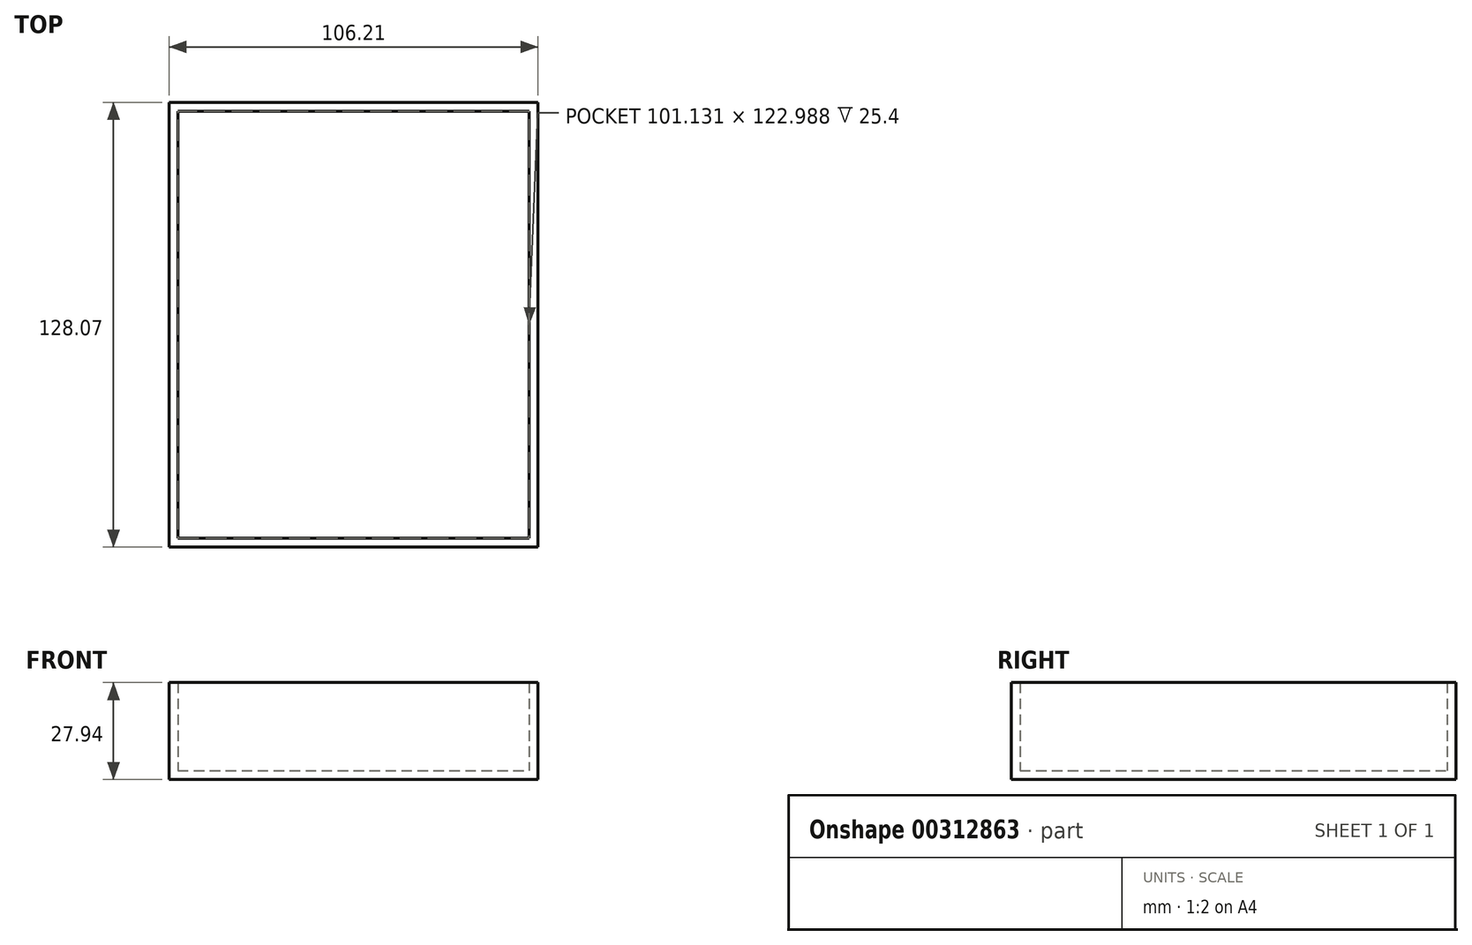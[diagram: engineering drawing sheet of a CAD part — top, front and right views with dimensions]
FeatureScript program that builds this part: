
annotation { "Feature Type Name" : "Feature", "Feature Type Description" : "" }
export const myFeature = defineFeature(function(context is Context, id is Id, definition is map)
    precondition{}
    {
        {
            var Q0;
            Q0=qCreatedBy(makeId("Top.planeOp"),FACE);
            var sketch = newSketch(context, id + "F0", { "sketchPlane" : qUnion([Q0])});
            skLineSegment(sketch, "E0.bottom", {"start": v(-112, 264.09) * mm, "end": v(0, 264.09) * mm});
            skLineSegment(sketch, "E0.top", {"start": v(-112, 291.18) * mm, "end": v(0, 291.18) * mm});
            skLineSegment(sketch, "E0.left", {"start": v(-112, 264.09) * mm, "end": v(-112, 291.18) * mm});
            skLineSegment(sketch, "E0.right", {"start": v(0, 264.09) * mm, "end": v(0, 291.18) * mm});
            skLineSegment(sketch, "E1.bottom", {"start": v(-61.53, 0) * mm, "end": v(39.6, 0) * mm});
            skLineSegment(sketch, "E1.top", {"start": v(-61.53, 122.99) * mm, "end": v(39.6, 122.99) * mm});
            skLineSegment(sketch, "E1.left", {"start": v(-61.53, 0) * mm, "end": v(-61.53, 122.99) * mm});
            skLineSegment(sketch, "E1.right", {"start": v(39.6, 0) * mm, "end": v(39.6, 122.99) * mm});
            skSolve(sketch);
        }
        {
            var Q0;
            Q0 = qSketchRegion(id + "F0", true);
            extrude(context, id + "F1", {"entities" : qUnion([Q0]), "depth" : 25.4 * mm});
        }
        {
            var Q0;
            Q0=makeQuery(id+"F1.opExtrude","SWEPT_BODY",BODY,{"disambiguationData":[OSD([sQuery(id+"F0.wireOp",EDGE,"E0.bottom"),sQuery(id+"F0.wireOp",EDGE,"E0.top"),sQuery(id+"F0.wireOp",EDGE,"E0.left"),sQuery(id+"F0.wireOp",EDGE,"E0.right")])]});
            deleteBodies(context, id + "F2", {"entities" : qUnion([Q0])});
        }
        {
            var Q0;
            Q0=makeQuery(id+"F1.opExtrude","CAP_FACE",FACE,{"disambiguationData":[OSD([sQuery(id+"F0.wireOp",EDGE,"E1.bottom"),sQuery(id+"F0.wireOp",EDGE,"E1.top"),sQuery(id+"F0.wireOp",EDGE,"E1.left"),sQuery(id+"F0.wireOp",EDGE,"E1.right")])],"isStart":false});
            shell(context, id + "F3", {"entities" : qUnion([Q0]), "thickness" : 2.54 * mm, "oppositeDirection" : true});
        }
    });
